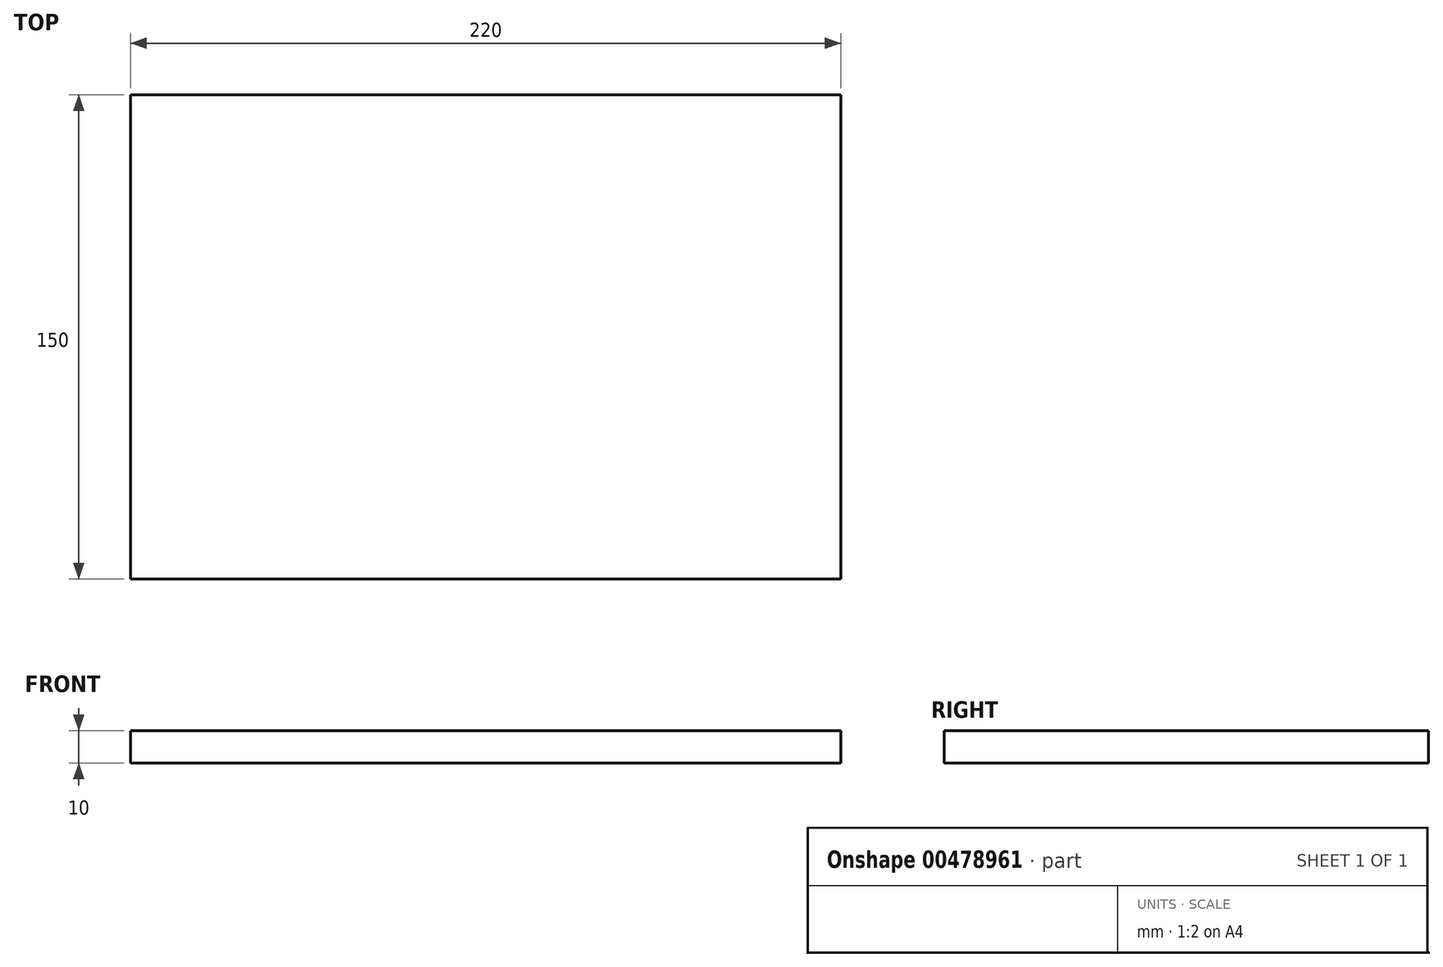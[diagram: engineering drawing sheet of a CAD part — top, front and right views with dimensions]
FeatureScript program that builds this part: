
annotation { "Feature Type Name" : "Feature", "Feature Type Description" : "" }
export const myFeature = defineFeature(function(context is Context, id is Id, definition is map)
    precondition{}
    {
        {
            var Q0;
            Q0=qCreatedBy(makeId("Top.planeOp"),FACE);
            var sketch = newSketch(context, id + "F0", { "sketchPlane" : qUnion([Q0])});
            skLineSegment(sketch, "E0.bottom", {"start": v(96.3, -75) * mm, "end": v(-123.7, -75) * mm});
            skLineSegment(sketch, "E0.top", {"start": v(96.3, 75) * mm, "end": v(-123.7, 75) * mm});
            skLineSegment(sketch, "E0.left", {"start": v(96.3, -75) * mm, "end": v(96.3, 75) * mm});
            skLineSegment(sketch, "E0.right", {"start": v(-123.7, -75) * mm, "end": v(-123.7, 75) * mm});
            skPoint(sketch, "E0.middle", {"position": v(-13.7, 0) * mm});
            skSolve(sketch);
        }
        {
            var Q0;
            Q0=makeQuery(id+"F0.imprint","IMPRINT",FACE,{"disambiguationData":[TD([[makeQuery(id+"F0.imprint","IMPRINT",EDGE,{"derivedFrom":sQuery(id+"F0.wireOp",EDGE,"E0.bottom")}),-1.0]])]});
            extrude(context, id + "F1", {"entities" : qUnion([Q0]), "depth" : 10 * mm});
        }
    });
